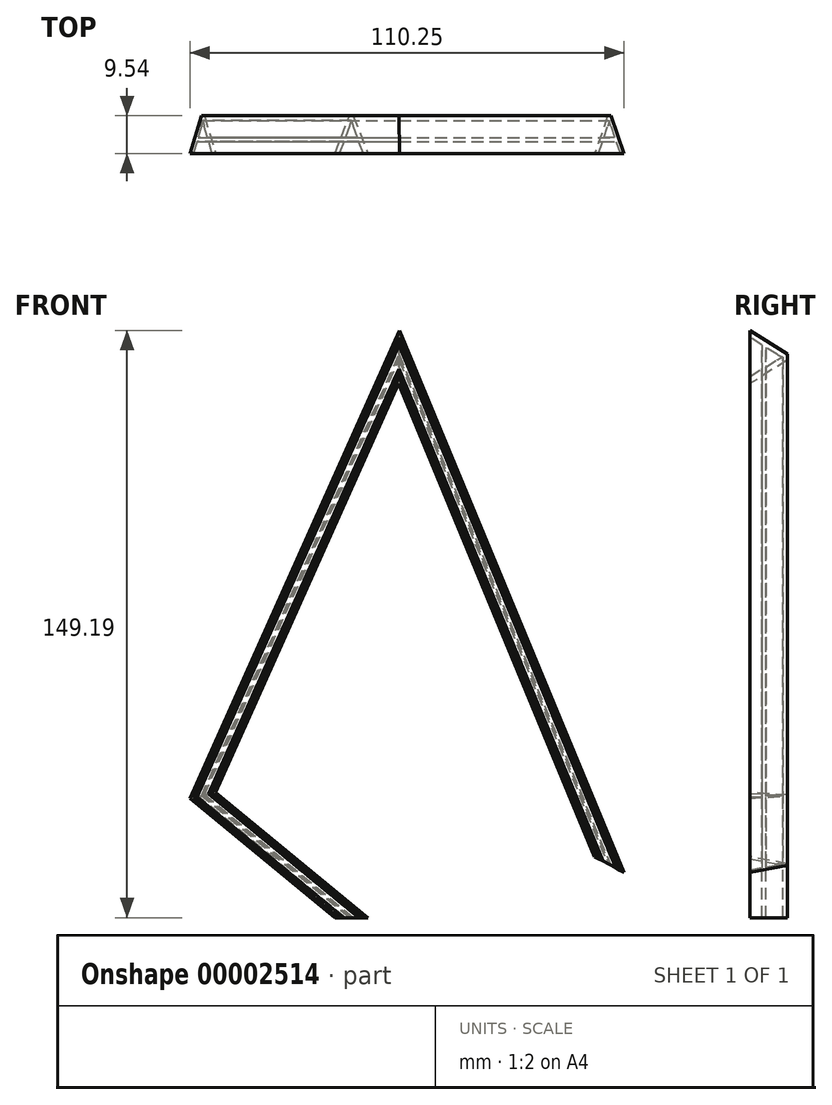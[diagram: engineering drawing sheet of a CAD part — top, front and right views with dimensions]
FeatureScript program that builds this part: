
annotation { "Feature Type Name" : "Feature", "Feature Type Description" : "" }
export const myFeature = defineFeature(function(context is Context, id is Id, definition is map)
    precondition{}
    {
        {
            var Q0;
            Q0=qCreatedBy(makeId("Top.planeOp"),FACE);
            var sketch = newSketch(context, id + "F0", { "sketchPlane" : qUnion([Q0])});
            skText(sketch, "E0", { "text": "A", "fontName": "OpenSans-Regular.ttf"});
            const initialGuessF0  = {"E0": [-0.01606, -0.00958, 1, 0, 0.00958]};
            skSetInitialGuess(sketch, initialGuessF0);
            skSolve(sketch);
        }
        {
            var Q0;
            Q0=qCreatedBy(makeId("Front.planeOp"),FACE);
            var sketch = newSketch(context, id + "F1", { "sketchPlane" : qUnion([Q0])});
            skLineSegment(sketch, "E1", {"start": v(0, 0) * mm, "end": v(-40.36, 33.22) * mm});
            skLineSegment(sketch, "E2", {"start": v(-40.36, 33.22) * mm, "end": v(0, 123.4) * mm});
            skLineSegment(sketch, "E3", {"start": v(0, 123.4) * mm, "end": v(43.22, 19.07) * mm});
            skSolve(sketch);
        }
        {
            var Q0;
            Q0 = qSketchRegion(id + "F0", true);
            var Q1;
            Q1=sQuery(id+"F1.wireOp",EDGE,"E1");
            var Q2;
            Q2=sQuery(id+"F1.wireOp",EDGE,"E2");
            var Q3;
            Q3=sQuery(id+"F1.wireOp",EDGE,"E3");
            sweep(context, id + "F2", {"profiles" : qUnion([Q0]), "path" : qUnion([Q1, Q2, Q3])});
        }
    });
